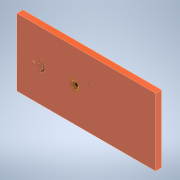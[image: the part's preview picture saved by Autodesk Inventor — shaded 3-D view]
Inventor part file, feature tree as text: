
AUTODESK INVENTOR PART (.ipt)
format: ipt  version: 2022.2 (Build 262287010, 287A)  size: 257,024 bytes
history: native  units: mm
features: extrude x14, sketch x5, plane x4, other x1
ambient origin geometry x8: Origin, YZ Plane, XZ Plane, XY Plane, X Axis, Y Axis, Z Axis, Center Point
bodies: Body1 (feature_tree)
feature tree (24):
  other  "Sólido1"
  extrude  "Extrusión1"  Depth=170.0mm
  plane  "Plano de trabajo4"
  plane  "Plano de trabajo1"
  extrude  "Extrusión10"  Depth=15.0mm
  extrude  "Extrusión11"  Depth=85.0mm
  extrude  "Extrusión12"  Depth=10.5mm
  plane  "Plano de trabajo2"
  extrude  "Extrusión14"  Depth=3.5mm
  plane  "Plano de trabajo3"
  extrude  "Extrusión22"  Depth=3.5mm
  extrude  "Extrusión23"  Depth=3.5mm
  extrude  "Extrusión24"  Depth=3.5mm
  extrude  "Extrusión25"  Depth=15.0mm
  extrude  "Extrusión26"  Depth=15.0mm
  sketch  "Boceto21"  dims[d29=50.0mm d31=35.0mm d32=134.19mm d35=40.0mm d36=25.0mm d51=15.0mm d59=15.0mm d60=12.5mm d61=6.0mm d62=12.5mm d63=6.0mm d64=3.0mm d65=3.0mm d66=1.5mm d67=0.0mm d68=3.0mm d69=3.0mm d70=0.0mm d71=0.0mm d72=5.0mm d73=0.0mm d77=10.0mm d78=0.0mm d79=0.0mm d80=148.0mm d82=40.0mm d87=80.0mm d88=30.0mm d102=35.0mm d115=90.0mm d116=15.0mm d117=0.0mm d118=0.0mm d119=0.0mm d121=5.0mm d122=0.0mm d126=15.0mm d127=6.0mm d128=6.0mm d129=1.5mm d130=1.5mm d131=1.5mm d132=0.0mm d133=0.0mm d134=0.0mm d135=3.0mm d139=125.81mm d141=7.5mm d146=20.0mm d147=20.0mm d148=15.0mm d149=0.0mm d150=5.0mm d151=0.0mm d152=5.0mm d153=0.0mm d154=0.0mm d155=3.5mm d156=0.0mm d44=0.5mm d45=0.872665mm d46=0.5mm d47=0.872665mm d74=0.5mm d75=0.872665mm d98=0.5mm d99=0.872665mm d100=0.5mm d101=0.872665mm d103=0.5mm d104=0.872665mm d105=0.5mm d106=0.872665mm d107=0.5mm d108=0.872665mm d109=0.5mm d110=0.872665mm d120=0.5mm d144=0.5mm d145=0.872665mm d157=0.5mm d158=0.872665mm d159=0.5mm d160=0.872665mm]
  extrude  "Extrusión28"  Depth=12.5mm
  extrude  "Extrusión29"  Depth=3.5mm
  extrude  "Extrusión30"  Depth=12.5mm
  extrude  "Extrusión31"  Depth=3.5mm
  sketch  "Boceto2"  dims[d0=260.0mm d1=170.0mm]
  sketch  "Boceto13"  dims[d2=15.0mm d3=0.0mm d7=5.25mm]
  sketch  "Boceto15"  dims[d8=19.75mm d14=85.0mm]
  sketch  "Boceto20"  dims[d23=10.5mm d25=5.25mm]
